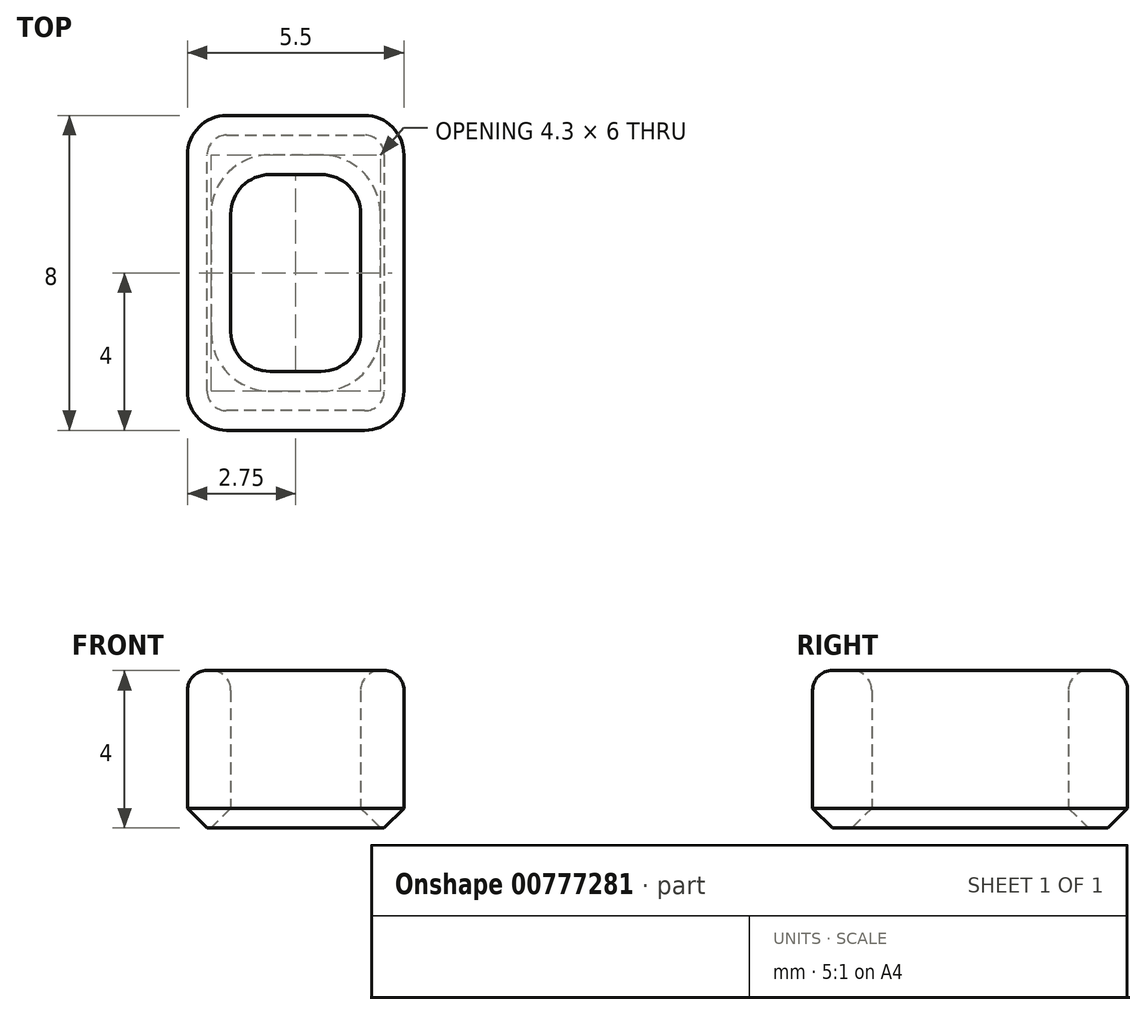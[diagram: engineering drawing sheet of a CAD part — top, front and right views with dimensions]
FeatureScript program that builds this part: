
annotation { "Feature Type Name" : "Feature", "Feature Type Description" : "" }
export const myFeature = defineFeature(function(context is Context, id is Id, definition is map)
    precondition{}
    {
        {
            var Q0;
            Q0=qCreatedBy(makeId("Top.planeOp"),FACE);
            var sketch = newSketch(context, id + "F0", { "sketchPlane" : qUnion([Q0])});
            skLineSegment(sketch, "E0.bottom", {"start": v(2.75, -4) * mm, "end": v(-2.75, -4) * mm});
            skLineSegment(sketch, "E0.top", {"start": v(2.75, 4) * mm, "end": v(-2.75, 4) * mm});
            skLineSegment(sketch, "E0.left", {"start": v(2.75, -4) * mm, "end": v(2.75, 4) * mm});
            skLineSegment(sketch, "E0.right", {"start": v(-2.75, -4) * mm, "end": v(-2.75, 4) * mm});
            skPoint(sketch, "E0.middle", {"position": v(0, 0) * mm});
            skLineSegment(sketch, "E1.bottom", {"start": v(1.65, -2.5) * mm, "end": v(-1.65, -2.5) * mm});
            skLineSegment(sketch, "E1.top", {"start": v(1.65, 2.5) * mm, "end": v(-1.65, 2.5) * mm});
            skLineSegment(sketch, "E1.left", {"start": v(1.65, -2.5) * mm, "end": v(1.65, 2.5) * mm});
            skLineSegment(sketch, "E1.right", {"start": v(-1.65, -2.5) * mm, "end": v(-1.65, 2.5) * mm});
            skSolve(sketch);
        }
        {
            var Q0;
            Q0=makeQuery(id+"F0.imprint","IMPRINT",FACE,{"disambiguationData":[TD([[makeQuery(id+"F0.imprint","IMPRINT",EDGE,{"derivedFrom":sQuery(id+"F0.wireOp",EDGE,"E0.bottom")}),-1.0]])]});
            extrude(context, id + "F1", {"entities" : qUnion([Q0]), "depth" : 4 * mm, "offsetDistance" : 25 * mm});
        }
        {
            var Q0;
            Q0=makeQuery(id+"F1.opExtrude","SWEPT_EDGE",EDGE,{"disambiguationData":[OSD([sQuery(id+"F0.wireOp",EDGE,"E0.bottom"),sQuery(id+"F0.wireOp",EDGE,"E0.right")])]});
            var Q1;
            Q1=makeQuery(id+"F1.opExtrude","SWEPT_EDGE",EDGE,{"disambiguationData":[OSD([sQuery(id+"F0.wireOp",EDGE,"E0.bottom"),sQuery(id+"F0.wireOp",EDGE,"E0.left")])]});
            var Q2;
            Q2=makeQuery(id+"F1.opExtrude","SWEPT_EDGE",EDGE,{"disambiguationData":[OSD([sQuery(id+"F0.wireOp",EDGE,"E0.top"),sQuery(id+"F0.wireOp",EDGE,"E0.right")])]});
            var Q3;
            Q3=makeQuery(id+"F1.opExtrude","SWEPT_EDGE",EDGE,{"disambiguationData":[OSD([sQuery(id+"F0.wireOp",EDGE,"E0.top"),sQuery(id+"F0.wireOp",EDGE,"E0.left")])]});
            fillet(context, id + "F2", {"entities" : qUnion([Q0, Q1, Q2, Q3]), "radius" : 1 * mm, "tangentPropagation" : true, "allowEdgeOverflow" : false});
        }
        {
            var Q0;
            Q0=makeQuery(id+"F1.opExtrude","SWEPT_EDGE",EDGE,{"disambiguationData":[OSD([sQuery(id+"F0.wireOp",EDGE,"E1.top"),sQuery(id+"F0.wireOp",EDGE,"E1.left")])]});
            var Q1;
            Q1=makeQuery(id+"F1.opExtrude","SWEPT_EDGE",EDGE,{"disambiguationData":[OSD([sQuery(id+"F0.wireOp",EDGE,"E1.bottom"),sQuery(id+"F0.wireOp",EDGE,"E1.left")])]});
            var Q2;
            Q2=makeQuery(id+"F1.opExtrude","SWEPT_EDGE",EDGE,{"disambiguationData":[OSD([sQuery(id+"F0.wireOp",EDGE,"E1.bottom"),sQuery(id+"F0.wireOp",EDGE,"E1.right")])]});
            var Q3;
            Q3=makeQuery(id+"F1.opExtrude","SWEPT_EDGE",EDGE,{"disambiguationData":[OSD([sQuery(id+"F0.wireOp",EDGE,"E1.top"),sQuery(id+"F0.wireOp",EDGE,"E1.right")])]});
            fillet(context, id + "F3", {"entities" : qUnion([Q0, Q1, Q2, Q3]), "radius" : 1 * mm, "tangentPropagation" : true, "allowEdgeOverflow" : false});
        }
        {
            var Q0;
            Q0=makeQuery(id+"F1.opExtrude","CAP_FACE",FACE,{"disambiguationData":[OSD([sQuery(id+"F0.wireOp",EDGE,"E0.bottom"),sQuery(id+"F0.wireOp",EDGE,"E0.top"),sQuery(id+"F0.wireOp",EDGE,"E0.left"),sQuery(id+"F0.wireOp",EDGE,"E0.right"),sQuery(id+"F0.wireOp",EDGE,"E1.bottom"),sQuery(id+"F0.wireOp",EDGE,"E1.top"),sQuery(id+"F0.wireOp",EDGE,"E1.left"),sQuery(id+"F0.wireOp",EDGE,"E1.right")])],"isStart":false});
            fillet(context, id + "F4", {"entities" : qUnion([Q0]), "radius" : 0.5 * mm, "tangentPropagation" : true, "allowEdgeOverflow" : false});
        }
        {
            var Q0;
            Q0=makeQuery(id+"F1.opExtrude","CAP_FACE",FACE,{"disambiguationData":[OSD([sQuery(id+"F0.wireOp",EDGE,"E0.bottom"),sQuery(id+"F0.wireOp",EDGE,"E0.top"),sQuery(id+"F0.wireOp",EDGE,"E0.left"),sQuery(id+"F0.wireOp",EDGE,"E0.right"),sQuery(id+"F0.wireOp",EDGE,"E1.bottom"),sQuery(id+"F0.wireOp",EDGE,"E1.top"),sQuery(id+"F0.wireOp",EDGE,"E1.left"),sQuery(id+"F0.wireOp",EDGE,"E1.right")])],"isStart":true});
            chamfer(context, id + "F5", {"entities" : qUnion([Q0]), "width" : 0.5 * mm, "tangentPropagation" : true});
        }
    });
